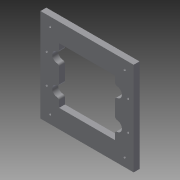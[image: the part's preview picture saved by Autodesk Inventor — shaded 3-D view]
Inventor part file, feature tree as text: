
AUTODESK INVENTOR PART (.ipt)
format: ipt  version: 2014 SP1 (Build 180222100, 222)  size: 138,240 bytes
history: native  units: mm
features: extrude x1, sketch x1
ambient origin geometry x8: Origin, YZ Plane, XZ Plane, XY Plane, X Axis, Y Axis, Z Axis, Center Point
bodies: Solid1 (feature_tree)
feature tree (2):
  extrude  "Extrusion1"  [1 undecoded]
  sketch  "Sketch1"  dims[d0=4.0mm d1=0.0mm]
note: 1 required parameter value undecoded (feature->parameter linkage not recoverable at this tier; creation-order binding heuristic only, values carry confidence <= 0.55)
